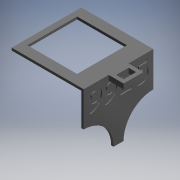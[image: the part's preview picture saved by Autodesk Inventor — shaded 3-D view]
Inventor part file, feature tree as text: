
AUTODESK INVENTOR PART (.ipt)
format: ipt  version: 2019 (Build 230136000, 136)  size: 369,152 bytes
history: native  units: mm (DEFAULTED — no unit token found)
features: extrude x5, sketch x5
ambient origin geometry x8: Origin, YZ Plane, XZ Plane, XY Plane, X Axis, Y Axis, Z Axis, Center Point
bodies: Solid1 (feature_tree)
feature tree (10):
  extrude  "Extrusion1"  Depth=88.9mm
  extrude  "Extrusion2"  Depth=63.5mm
  extrude  "Extrusion3"  Depth=12.7mm
  extrude  "Extrusion5"  Depth=3.175mm
  extrude  "Extrusion6"  Depth=88.9mm
  sketch  "Sketch1"  dims[d0=88.9mm d1=88.9mm]
  sketch  "Sketch2"  dims[d2=63.5mm d3=63.5mm]
  sketch  "Sketch3"  dims[d4=18.034mm d5=12.7mm]
  sketch  "Sketch6"  dims[d6=3.175mm d7=0.0mm d8=82.55mm]
  sketch  "Sketch7"  dims[d9=88.9mm d10=88.9mm d11=3.175mm d12=0.0mm d13=1.27mm d14=0.0mm d23=19.05mm d24=25.4mm d25=88.9mm d26=31.75mm d27=4.7625mm d28=4.7625mm d29=4.7625mm d30=4.7625mm d31=6.35mm d32=0.0mm d33=76.2mm d34=76.2mm d35=25.4mm d36=0.0mm]
